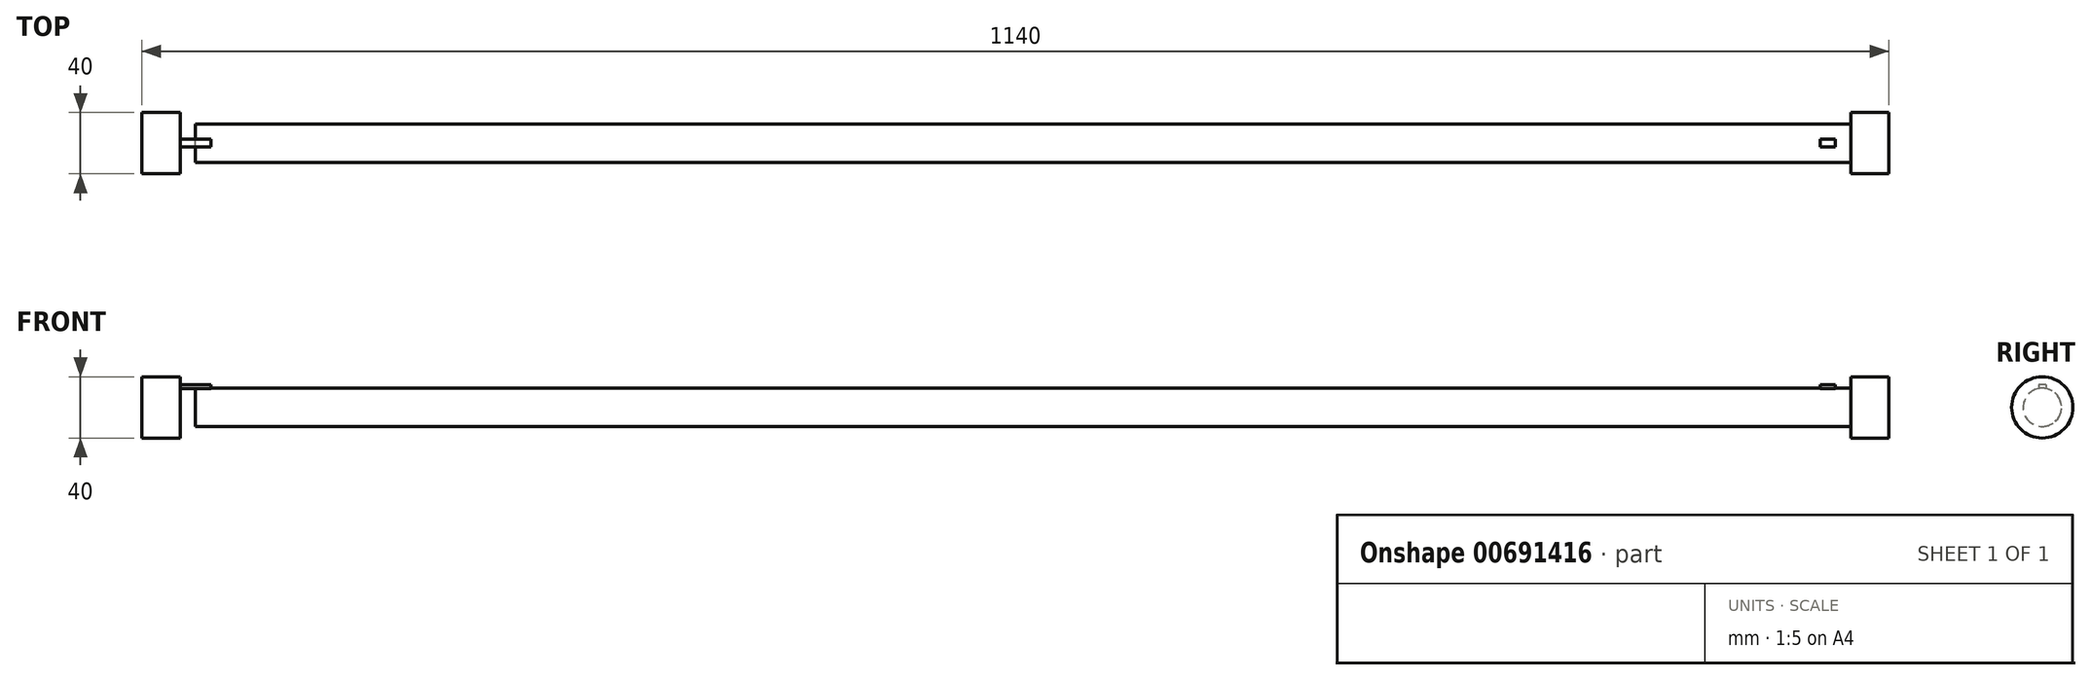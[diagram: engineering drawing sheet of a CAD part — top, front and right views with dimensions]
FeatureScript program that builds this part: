
annotation { "Feature Type Name" : "Feature", "Feature Type Description" : "" }
export const myFeature = defineFeature(function(context is Context, id is Id, definition is map)
    precondition{}
    {
        {
            var Q0;
            Q0=qCreatedBy(makeId("Right.planeOp"),FACE);
            var sketch = newSketch(context, id + "F0", { "sketchPlane" : qUnion([Q0])});
            skLineSegment(sketch, "E0.bottom", {"start": v(2.5, 1.25) * mm, "end": v(-2.5, 1.25) * mm});
            skLineSegment(sketch, "E0.top", {"start": v(2.5, -1.25) * mm, "end": v(-2.5, -1.25) * mm});
            skLineSegment(sketch, "E0.left", {"start": v(2.5, 1.25) * mm, "end": v(2.5, -1.25) * mm});
            skLineSegment(sketch, "E0.right", {"start": v(-2.5, 1.25) * mm, "end": v(-2.5, -1.25) * mm});
            skPoint(sketch, "E0.middle", {"position": v(0, 0) * mm});
            skArc(sketch, "E1", {"start": v(-2.5, -1.25) * mm, "mid": v(0, -26) * mm, "end": v(2.5, -1.25) * mm});
            skSolve(sketch);
        }
        {
            var Q0;
            Q0 = qSketchRegion(id + "F0", true);
            extrude(context, id + "F1", {"entities" : qUnion([Q0]), "depth" : 10 * mm, "offsetDistance" : 25 * mm});
        }
        {
            var Q0;
            Q0=makeQuery(id+"F1.opExtrude","CAP_FACE",FACE,{"disambiguationData":[OSD([sQuery(id+"F0.wireOp",EDGE,"E0.bottom"),sQuery(id+"F0.wireOp",EDGE,"E0.left"),sQuery(id+"F0.wireOp",EDGE,"E0.right"),sQuery(id+"F0.wireOp",EDGE,"E1")])],"isStart":false});
            var sketch = newSketch(context, id + "F2", { "sketchPlane" : qUnion([Q0])});
            skCircle(sketch, "E2", {"center": v(0, -13.5) * mm, "radius": 12.5 * mm});
            skSolve(sketch);
        }
        {
            var Q0;
            {var subQ0=sQuery(id+"F2.wireOp",EDGE,"E2");var subQ1=makeQuery(id+"F2.imprint","INTERSECT",VERTEX,{"derivedFrom":[makeQuery(id+"F1.opExtrude","CAP_EDGE",EDGE,{"disambiguationData":[OSD([sQuery(id+"F0.wireOp",EDGE,"E0.left")])],"isStart":false}),subQ0]});Q0=makeQuery(id+"F2.imprint","IMPRINT",FACE,{"disambiguationData":[TD([[makeQuery(id+"F2.imprint","IMPRINT",EDGE,{"disambiguationData":[TD([[subQ1,1.0]])],"derivedFrom":subQ0}),1.0]])]});}
            extrude(context, id + "F3", {"entities" : qUnion([Q0]), "operationType" : NewBodyOperationType.ADD, "depth" : 1040 * mm, "offsetDistance" : 25 * mm});
        }
        {
            var Q0;
            Q0=makeQuery(id+"F3.opExtrude","CAP_FACE",FACE,{"disambiguationData":[OSD([sQuery(id+"F2.wireOp",EDGE,"E2")])],"isStart":false});
            var sketch = newSketch(context, id + "F4", { "sketchPlane" : qUnion([Q0])});
            skCircle(sketch, "E3", {"center": v(0, -13.5) * mm, "radius": 12.5 * mm});
            skSolve(sketch);
        }
        {
            var Q0;
            Q0 = qSketchRegion(id + "F4", true);
            extrude(context, id + "F5", {"entities" : qUnion([Q0]), "operationType" : NewBodyOperationType.ADD, "depth" : 10 * mm, "offsetDistance" : 25 * mm});
        }
        {
            var Q0;
            Q0=makeQuery(id+"F5.opExtrude","CAP_FACE",FACE,{"disambiguationData":[OSD([sQuery(id+"F4.wireOp",EDGE,"E3")])],"isStart":false});
            var sketch = newSketch(context, id + "F6", { "sketchPlane" : qUnion([Q0])});
            skLineSegment(sketch, "E4.bottom", {"start": v(2.5, 1.25) * mm, "end": v(-2.5, 1.25) * mm});
            skLineSegment(sketch, "E4.top", {"start": v(2.5, -1.25) * mm, "end": v(-2.5, -1.25) * mm});
            skLineSegment(sketch, "E4.left", {"start": v(2.5, 1.25) * mm, "end": v(2.5, -1.25) * mm});
            skLineSegment(sketch, "E4.right", {"start": v(-2.5, 1.25) * mm, "end": v(-2.5, -1.25) * mm});
            skPoint(sketch, "E4.middle", {"position": v(0, 0) * mm});
            skArc(sketch, "E5", {"start": v(-2.5, -1.25) * mm, "mid": v(0, -26) * mm, "end": v(2.5, -1.25) * mm});
            skSolve(sketch);
        }
        {
            var Q0;
            Q0 = qSketchRegion(id + "F6", true);
            extrude(context, id + "F7", {"entities" : qUnion([Q0]), "operationType" : NewBodyOperationType.ADD, "depth" : 10 * mm, "offsetDistance" : 25 * mm});
        }
        {
            var Q0;
            Q0=makeQuery(id+"F7.opExtrude","CAP_FACE",FACE,{"disambiguationData":[OSD([sQuery(id+"F6.wireOp",EDGE,"E4.bottom"),sQuery(id+"F6.wireOp",EDGE,"E4.left"),sQuery(id+"F6.wireOp",EDGE,"E4.right"),sQuery(id+"F6.wireOp",EDGE,"E5")])],"isStart":false});
            var sketch = newSketch(context, id + "F8", { "sketchPlane" : qUnion([Q0])});
            skCircle(sketch, "E6", {"center": v(0, -13.5) * mm, "radius": 12.5 * mm});
            skSolve(sketch);
        }
        {
            var Q0;
            Q0 = qSketchRegion(id + "F8", true);
            extrude(context, id + "F9", {"entities" : qUnion([Q0]), "operationType" : NewBodyOperationType.ADD, "depth" : 10 * mm, "offsetDistance" : 25 * mm});
        }
        {
            var Q0;
            Q0=makeQuery(id+"F1.opExtrude","CAP_FACE",FACE,{"disambiguationData":[OSD([sQuery(id+"F0.wireOp",EDGE,"E0.bottom"),sQuery(id+"F0.wireOp",EDGE,"E0.left"),sQuery(id+"F0.wireOp",EDGE,"E0.right"),sQuery(id+"F0.wireOp",EDGE,"E1")])],"isStart":true});
            var sketch = newSketch(context, id + "F10", { "sketchPlane" : qUnion([Q0])});
            skCircle(sketch, "E7", {"center": v(0, -13.5) * mm, "radius": 12.5 * mm});
            skSolve(sketch);
        }
        {
            var Q0;
            {var subQ0=sQuery(id+"F10.wireOp",EDGE,"E7");Q0=makeQuery(id+"F10.imprint","IMPRINT",FACE,{"disambiguationData":[TD([[makeQuery(id+"F10.imprint","IMPRINT",EDGE,{"disambiguationData":[OD(0.0)],"derivedFrom":subQ0}),-1.0]])]});}
            extrude(context, id + "F11", {"entities" : qUnion([Q0]), "operationType" : NewBodyOperationType.ADD, "depth" : 10 * mm, "offsetDistance" : 25 * mm});
        }
        {
            var Q0;
            Q0=makeQuery(id+"F11.opExtrude","CAP_FACE",FACE,{"disambiguationData":[OSD([sQuery(id+"F10.wireOp",EDGE,"E7")])],"isStart":false});
            var sketch = newSketch(context, id + "F12", { "sketchPlane" : qUnion([Q0])});
            skCircle(sketch, "E8", {"center": v(0, -13.5) * mm, "radius": 20 * mm});
            skSolve(sketch);
        }
        {
            var Q0;
            Q0 = qSketchRegion(id + "F12", true);
            extrude(context, id + "F13", {"entities" : qUnion([Q0]), "operationType" : NewBodyOperationType.ADD, "depth" : 25 * mm, "offsetDistance" : 25 * mm});
        }
        {
            var Q0;
            Q0=makeQuery(id+"F9.opExtrude","CAP_FACE",FACE,{"disambiguationData":[OSD([sQuery(id+"F8.wireOp",EDGE,"E6")])],"isStart":false});
            var sketch = newSketch(context, id + "F14", { "sketchPlane" : qUnion([Q0])});
            skCircle(sketch, "E9", {"center": v(0, -13.5) * mm, "radius": 20 * mm});
            skSolve(sketch);
        }
        {
            var Q0;
            Q0 = qSketchRegion(id + "F14", true);
            extrude(context, id + "F15", {"entities" : qUnion([Q0]), "operationType" : NewBodyOperationType.ADD, "depth" : 25 * mm, "offsetDistance" : 25 * mm});
        }
    });
